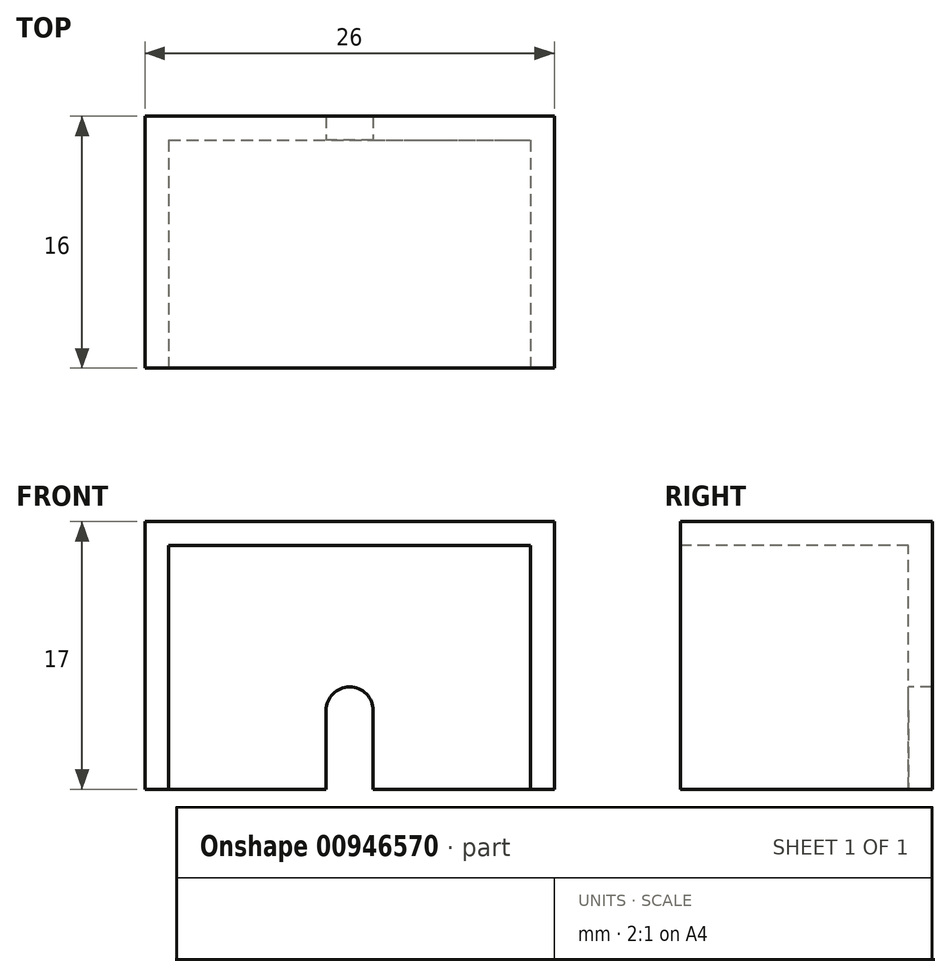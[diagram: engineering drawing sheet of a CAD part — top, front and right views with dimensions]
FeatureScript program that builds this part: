
annotation { "Feature Type Name" : "Feature", "Feature Type Description" : "" }
export const myFeature = defineFeature(function(context is Context, id is Id, definition is map)
    precondition{}
    {
        {
            var Q0;
            Q0=qCreatedBy(makeId("Front.planeOp"),FACE);
            var sketch = newSketch(context, id + "F0", { "sketchPlane" : qUnion([Q0])});
            skLineSegment(sketch, "E0.bottom", {"start": v(0, 0) * mm, "end": v(26, 0) * mm});
            skLineSegment(sketch, "E0.top", {"start": v(0, 17) * mm, "end": v(26, 17) * mm});
            skLineSegment(sketch, "E0.left", {"start": v(0, 0) * mm, "end": v(0, 17) * mm});
            skLineSegment(sketch, "E0.right", {"start": v(26, 0) * mm, "end": v(26, 17) * mm});
            skSolve(sketch);
        }
        {
            var Q0;
            Q0 = qSketchRegion(id + "F0", true);
            extrude(context, id + "F1", {"entities" : qUnion([Q0]), "oppositeDirection" : true, "depth" : 16 * mm, "offsetDistance" : 25 * mm});
        }
        {
            var Q0;
            Q0=qCreatedBy(makeId("Front.planeOp"),FACE);
            var sketch = newSketch(context, id + "F2", { "sketchPlane" : qUnion([Q0])});
            skPoint(sketch, "E1.0", {"position": v(13, 17) * mm});
            skPoint(sketch, "E2.0", {"position": v(13, 0) * mm});
            skLineSegment(sketch, "E3", {"start": v(13, 17) * mm, "end": v(13, 0) * mm, "construction": true});
            skLineSegment(sketch, "E4.bottom", {"start": v(1.5, 0) * mm, "end": v(24.5, 0) * mm});
            skLineSegment(sketch, "E4.top", {"start": v(1.5, 15.5) * mm, "end": v(24.5, 15.5) * mm});
            skLineSegment(sketch, "E4.left", {"start": v(1.5, 0) * mm, "end": v(1.5, 15.5) * mm});
            skLineSegment(sketch, "E4.right", {"start": v(24.5, 0) * mm, "end": v(24.5, 15.5) * mm});
            skSolve(sketch);
        }
        {
            var Q0;
            Q0 = qSketchRegion(id + "F2", true);
            extrude(context, id + "F3", {"entities" : qUnion([Q0]), "operationType" : NewBodyOperationType.REMOVE, "oppositeDirection" : true, "depth" : 14.5 * mm, "offsetDistance" : 25 * mm});
        }
        {
            var Q0;
            Q0=qCreatedBy(makeId("Front.planeOp"),FACE);
            var sketch = newSketch(context, id + "F4", { "sketchPlane" : qUnion([Q0])});
            skLineSegment(sketch, "E5.0", {"start": v(13, 17) * mm, "end": v(13, 0) * mm, "construction": true});
            skArc(sketch, "E6", {"start": v(14.5, 5) * mm, "mid": v(13, 6.5) * mm, "end": v(11.5, 5) * mm});
            skLineSegment(sketch, "E7.top", {"start": v(11.5, 0) * mm, "end": v(14.5, 0) * mm});
            skLineSegment(sketch, "E7.left", {"start": v(11.5, 5) * mm, "end": v(11.5, 0) * mm});
            skLineSegment(sketch, "E7.right", {"start": v(14.5, 5) * mm, "end": v(14.5, 0) * mm});
            skLineSegment(sketch, "E8.0", {"start": v(0, 0) * mm, "end": v(1.5, 0) * mm, "construction": true});
            skSolve(sketch);
        }
        {
            var Q0;
            Q0 = qSketchRegion(id + "F4", true);
            extrude(context, id + "F5", {"entities" : qUnion([Q0]), "operationType" : NewBodyOperationType.REMOVE, "oppositeDirection" : true, "depth" : 25 * mm, "offsetDistance" : 25 * mm});
        }
    });
